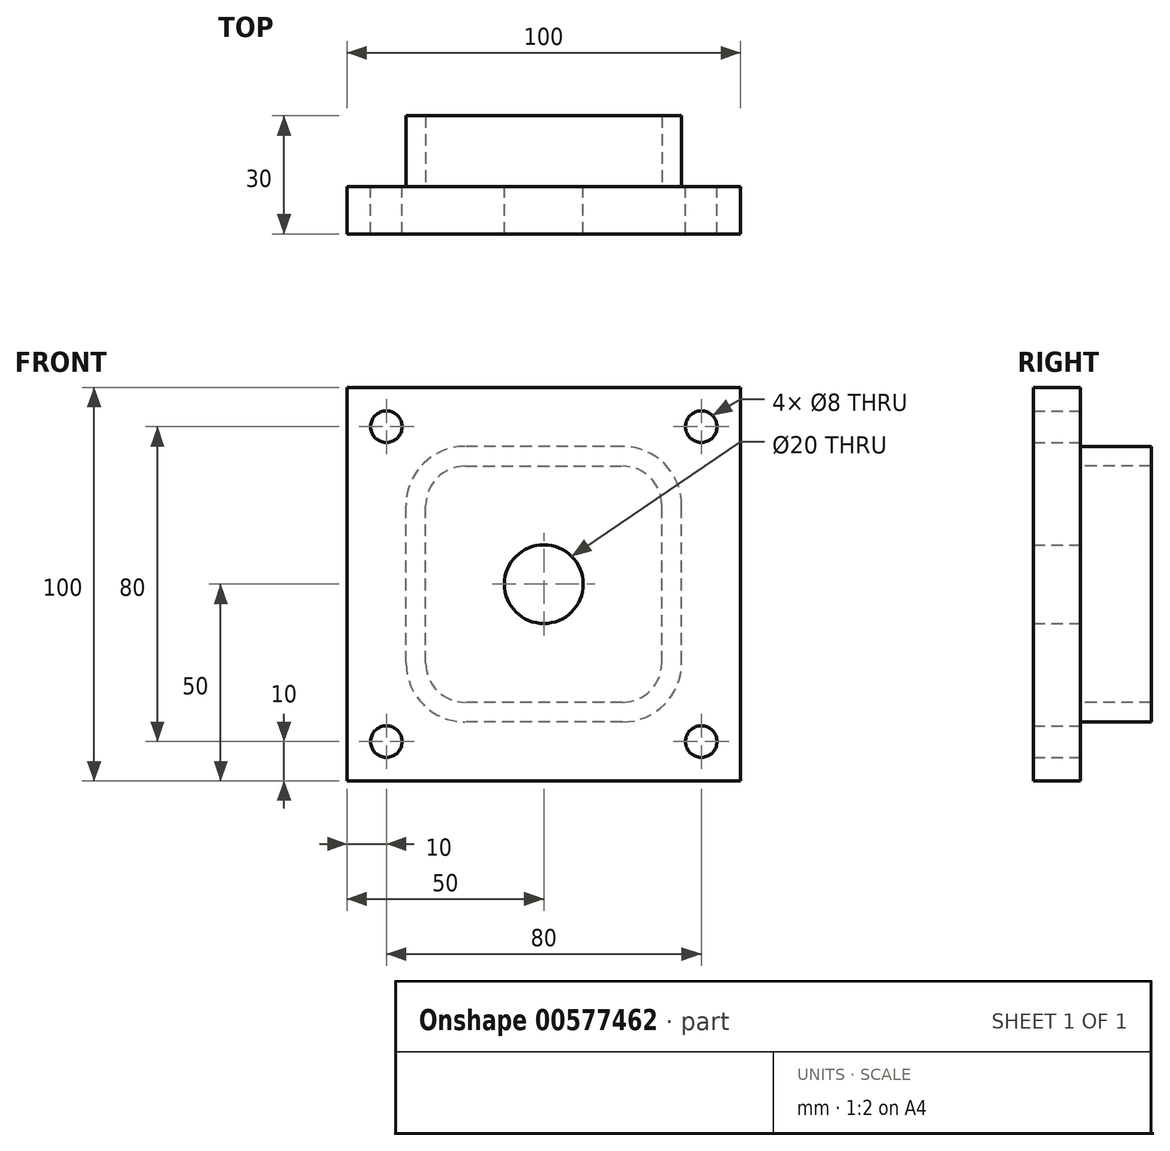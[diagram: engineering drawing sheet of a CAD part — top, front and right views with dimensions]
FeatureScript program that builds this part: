
annotation { "Feature Type Name" : "Feature", "Feature Type Description" : "" }
export const myFeature = defineFeature(function(context is Context, id is Id, definition is map)
    precondition{}
    {
        {
            var Q0;
            Q0=qCreatedBy(makeId("Front.planeOp"),FACE);
            var sketch = newSketch(context, id + "F0", { "sketchPlane" : qUnion([Q0])});
            skLineSegment(sketch, "E0", {"start": v(0, 0) * mm, "end": v(100, 0) * mm});
            skLineSegment(sketch, "E1", {"start": v(100, 0) * mm, "end": v(100, -100) * mm});
            skLineSegment(sketch, "E2", {"start": v(100, -100) * mm, "end": v(0, -100) * mm});
            skLineSegment(sketch, "E3", {"start": v(0, -100) * mm, "end": v(0, 0) * mm});
            skSolve(sketch);
        }
        {
            var Q0;
            Q0=makeQuery(id+"F0.imprint","IMPRINT",FACE,{"disambiguationData":[TD([[makeQuery(id+"F0.imprint","IMPRINT",EDGE,{"derivedFrom":sQuery(id+"F0.wireOp",EDGE,"E0")}),-1.0]])]});
            extrude(context, id + "F1", {"entities" : qUnion([Q0]), "depth" : 12 * mm, "offsetDistance" : 25 * mm});
        }
        {
            var Q0;
            Q0=makeQuery(id+"F1.opExtrude","CAP_FACE",FACE,{"disambiguationData":[OSD([sQuery(id+"F0.wireOp",EDGE,"E0"),sQuery(id+"F0.wireOp",EDGE,"E1"),sQuery(id+"F0.wireOp",EDGE,"E2"),sQuery(id+"F0.wireOp",EDGE,"E3")])],"isStart":true});
            var sketch = newSketch(context, id + "F2", { "sketchPlane" : qUnion([Q0])});
            skCircle(sketch, "E4", {"center": v(-90, -90) * mm, "radius": 4 * mm});
            skCircle(sketch, "E5", {"center": v(-90, -10) * mm, "radius": 4 * mm});
            skCircle(sketch, "E6", {"center": v(-10, -90) * mm, "radius": 4 * mm});
            skCircle(sketch, "E7", {"center": v(-10, -10) * mm, "radius": 4 * mm});
            skSolve(sketch);
        }
        {
            var Q0;
            Q0=makeQuery(id+"F2.imprint","IMPRINT",FACE,{"disambiguationData":[TD([[makeQuery(id+"F2.imprint","IMPRINT",EDGE,{"derivedFrom":sQuery(id+"F2.wireOp",EDGE,"E4")}),1.0]])]});
            var Q1;
            Q1=makeQuery(id+"F2.imprint","IMPRINT",FACE,{"disambiguationData":[TD([[makeQuery(id+"F2.imprint","IMPRINT",EDGE,{"derivedFrom":sQuery(id+"F2.wireOp",EDGE,"E6")}),1.0]])]});
            var Q2;
            Q2=makeQuery(id+"F2.imprint","IMPRINT",FACE,{"disambiguationData":[TD([[makeQuery(id+"F2.imprint","IMPRINT",EDGE,{"derivedFrom":sQuery(id+"F2.wireOp",EDGE,"E7")}),1.0]])]});
            var Q3;
            Q3=makeQuery(id+"F2.imprint","IMPRINT",FACE,{"disambiguationData":[TD([[makeQuery(id+"F2.imprint","IMPRINT",EDGE,{"derivedFrom":sQuery(id+"F2.wireOp",EDGE,"E5")}),1.0]])]});
            extrude(context, id + "F3", {"entities" : qUnion([Q0, Q1, Q2, Q3]), "operationType" : NewBodyOperationType.REMOVE, "oppositeDirection" : true, "depth" : 12 * mm, "offsetDistance" : 25 * mm});
        }
        {
            var Q0;
            Q0=makeQuery(id+"F1.opExtrude","CAP_FACE",FACE,{"disambiguationData":[OSD([sQuery(id+"F0.wireOp",EDGE,"E0"),sQuery(id+"F0.wireOp",EDGE,"E1"),sQuery(id+"F0.wireOp",EDGE,"E2"),sQuery(id+"F0.wireOp",EDGE,"E3")])],"isStart":true});
            var sketch = newSketch(context, id + "F4", { "sketchPlane" : qUnion([Q0])});
            skCircle(sketch, "E8", {"center": v(-50, -50) * mm, "radius": 10 * mm});
            skLineSegment(sketch, "E9", {"start": v(-70, -80) * mm, "end": v(-30, -80) * mm});
            skLineSegment(sketch, "E10", {"start": v(-30, -20) * mm, "end": v(-70, -20) * mm});
            skArc(sketch, "E11", {"start": v(-80, -70) * mm, "mid": v(-77.07, -77.07) * mm, "end": v(-70, -80) * mm});
            skLineSegment(sketch, "E12", {"start": v(-20, -70) * mm, "end": v(-20, -30) * mm});
            skArc(sketch, "E13", {"start": v(-30, -80) * mm, "mid": v(-22.93, -77.07) * mm, "end": v(-20, -70) * mm});
            skArc(sketch, "E14", {"start": v(-20, -30) * mm, "mid": v(-22.93, -22.93) * mm, "end": v(-30, -20) * mm});
            skLineSegment(sketch, "E15", {"start": v(-80, -70) * mm, "end": v(-80, -30) * mm});
            skArc(sketch, "E16", {"start": v(-70, -20) * mm, "mid": v(-77.07, -22.93) * mm, "end": v(-80, -30) * mm});
            skLineSegment(sketch, "E17", {"start": v(-70, -85) * mm, "end": v(-30, -85) * mm});
            skLineSegment(sketch, "E18", {"start": v(-15, -70) * mm, "end": v(-15, -30) * mm});
            skLineSegment(sketch, "E19", {"start": v(-70, -15) * mm, "end": v(-30, -15) * mm});
            skLineSegment(sketch, "E20", {"start": v(-85, -70) * mm, "end": v(-85, -30) * mm});
            skArc(sketch, "E21", {"start": v(-70, -15) * mm, "mid": v(-80.6, -19.4) * mm, "end": v(-85, -30) * mm});
            skArc(sketch, "E22", {"start": v(-85, -70) * mm, "mid": v(-80.6, -80.6) * mm, "end": v(-70, -85) * mm});
            skArc(sketch, "E23", {"start": v(-30, -85) * mm, "mid": v(-19.4, -80.6) * mm, "end": v(-15, -70) * mm});
            skArc(sketch, "E24", {"start": v(-15, -30) * mm, "mid": v(-19.4, -19.4) * mm, "end": v(-30, -15) * mm});
            skSolve(sketch);
        }
        {
            var Q0;
            Q0=makeQuery(id+"F4.imprint","IMPRINT",FACE,{"disambiguationData":[TD([[makeQuery(id+"F4.imprint","IMPRINT",EDGE,{"derivedFrom":sQuery(id+"F4.wireOp",EDGE,"E9")}),-1.0]])]});
            extrude(context, id + "F5", {"entities" : qUnion([Q0]), "operationType" : NewBodyOperationType.ADD, "depth" : 18 * mm, "offsetDistance" : 25 * mm});
        }
        {
            var Q0;
            Q0=makeQuery(id+"F4.imprint","IMPRINT",FACE,{"disambiguationData":[TD([[makeQuery(id+"F4.imprint","IMPRINT",EDGE,{"derivedFrom":sQuery(id+"F4.wireOp",EDGE,"E8")}),1.0]])]});
            var Q1;
            Q1=sQuery(id+"F4.wireOp",EDGE,"E8");
            extrude(context, id + "F6", {"entities" : qUnion([Q0]), "operationType" : NewBodyOperationType.REMOVE, "surfaceEntities" : qUnion([Q1]), "oppositeDirection" : true, "depth" : 18 * mm, "offsetDistance" : 25 * mm});
        }
    });
